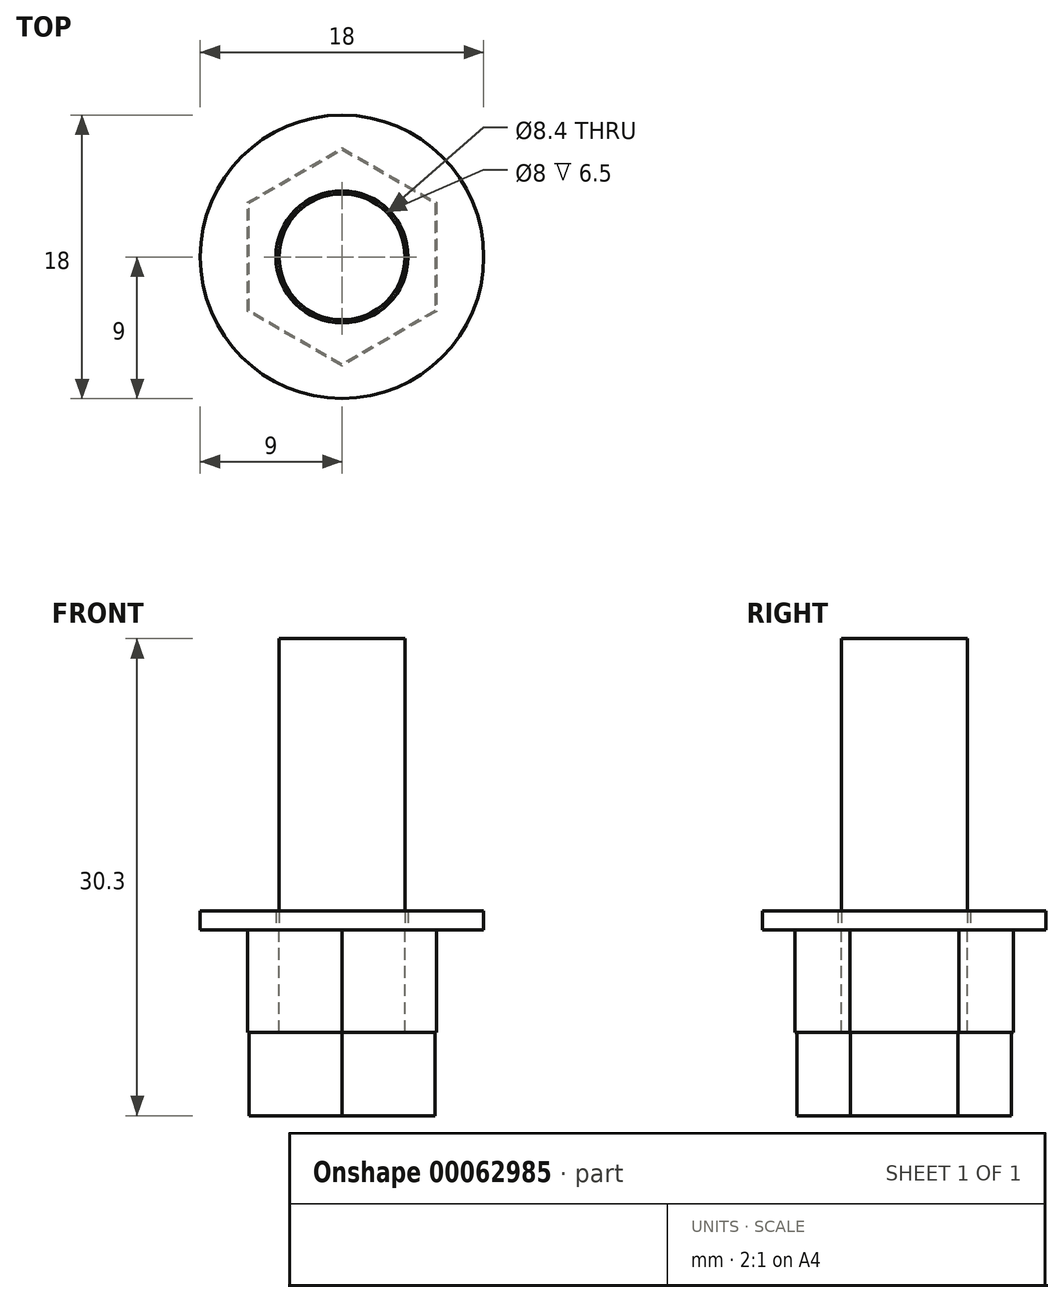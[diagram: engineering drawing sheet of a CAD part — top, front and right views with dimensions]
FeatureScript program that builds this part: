
annotation { "Feature Type Name" : "Feature", "Feature Type Description" : "" }
export const myFeature = defineFeature(function(context is Context, id is Id, definition is map)
    precondition{}
    {
        {
            var Q0;
            Q0=qCreatedBy(makeId("Top.planeOp"),FACE);
            var sketch = newSketch(context, id + "F0", { "sketchPlane" : qUnion([Q0])});
            skCircle(sketch, "E0.cCircle", {"center": v(0, 0) * mm, "radius": 5.9 * mm, "construction": true});
            skLineSegment(sketch, "E0.0", {"start": v(5.9, -3.4) * mm, "end": v(0, -6.81) * mm});
            skLineSegment(sketch, "E0.1", {"start": v(0, -6.81) * mm, "end": v(-5.9, -3.4) * mm});
            skLineSegment(sketch, "E0.2", {"start": v(-5.9, -3.4) * mm, "end": v(-5.9, 3.4) * mm});
            skLineSegment(sketch, "E0.3", {"start": v(-5.9, 3.4) * mm, "end": v(0, 6.81) * mm});
            skLineSegment(sketch, "E0.4", {"start": v(0, 6.81) * mm, "end": v(5.9, 3.4) * mm});
            skLineSegment(sketch, "E0.5", {"start": v(5.9, 3.4) * mm, "end": v(5.9, -3.4) * mm});
            skPoint(sketch, "E0.0.midPoint", {"position": v(2.95, -5.1) * mm});
            skSolve(sketch);
        }
        {
            var Q0;
            Q0=makeQuery(id+"F0.imprint","IMPRINT",FACE,{"disambiguationData":[TD([[makeQuery(id+"F0.imprint","IMPRINT",EDGE,{"derivedFrom":sQuery(id+"F0.wireOp",EDGE,"E0.0")}),-1.0]])]});
            extrude(context, id + "F1", {"entities" : qUnion([Q0]), "depth" : 5.3 * mm});
        }
        {
            var Q0;
            Q0=makeQuery(id+"F1.opExtrude","CAP_FACE",FACE,{"disambiguationData":[OSD([sQuery(id+"F0.wireOp",EDGE,"E0.0"),sQuery(id+"F0.wireOp",EDGE,"E0.1"),sQuery(id+"F0.wireOp",EDGE,"E0.2"),sQuery(id+"F0.wireOp",EDGE,"E0.3"),sQuery(id+"F0.wireOp",EDGE,"E0.4"),sQuery(id+"F0.wireOp",EDGE,"E0.5")])],"isStart":false});
            var sketch = newSketch(context, id + "F2", { "sketchPlane" : qUnion([Q0])});
            skCircle(sketch, "E1", {"center": v(0, 0) * mm, "radius": 4 * mm});
            skSolve(sketch);
        }
        {
            var Q0;
            Q0 = qSketchRegion(id + "F2", true);
            extrude(context, id + "F3", {"entities" : qUnion([Q0]), "operationType" : NewBodyOperationType.ADD, "depth" : 25 * mm});
        }
        {
            var Q0;
            Q0=makeQuery(id+"F1.opExtrude","CAP_FACE",FACE,{"disambiguationData":[OSD([sQuery(id+"F0.wireOp",EDGE,"E0.0"),sQuery(id+"F0.wireOp",EDGE,"E0.1"),sQuery(id+"F0.wireOp",EDGE,"E0.2"),sQuery(id+"F0.wireOp",EDGE,"E0.3"),sQuery(id+"F0.wireOp",EDGE,"E0.4"),sQuery(id+"F0.wireOp",EDGE,"E0.5")])],"isStart":false});
            var sketch = newSketch(context, id + "F4", { "sketchPlane" : qUnion([Q0])});
            skCircle(sketch, "E2.cCircle", {"center": v(0, 0) * mm, "radius": 6 * mm, "construction": true});
            skLineSegment(sketch, "E2.0", {"start": v(6, -3.46) * mm, "end": v(0, -6.93) * mm});
            skLineSegment(sketch, "E2.1", {"start": v(0, -6.93) * mm, "end": v(-6, -3.46) * mm});
            skLineSegment(sketch, "E2.2", {"start": v(-6, -3.46) * mm, "end": v(-6, 3.46) * mm});
            skLineSegment(sketch, "E2.3", {"start": v(-6, 3.46) * mm, "end": v(0, 6.93) * mm});
            skLineSegment(sketch, "E2.4", {"start": v(0, 6.93) * mm, "end": v(6, 3.46) * mm});
            skLineSegment(sketch, "E2.5", {"start": v(6, 3.46) * mm, "end": v(6, -3.46) * mm});
            skPoint(sketch, "E2.0.midPoint", {"position": v(3, -5.2) * mm});
            skSolve(sketch);
        }
        {
            var Q0;
            Q0 = qSketchRegion(id + "F4", true);
            extrude(context, id + "F5", {"entities" : qUnion([Q0]), "depth" : 6.5 * mm});
        }
        {
            var Q0;
            Q0=makeQuery(id+"F5.opExtrude","CAP_FACE",FACE,{"disambiguationData":[OSD([sQuery(id+"F4.wireOp",EDGE,"E2.0"),sQuery(id+"F4.wireOp",EDGE,"E2.1"),sQuery(id+"F4.wireOp",EDGE,"E2.2"),sQuery(id+"F4.wireOp",EDGE,"E2.3"),sQuery(id+"F4.wireOp",EDGE,"E2.4"),sQuery(id+"F4.wireOp",EDGE,"E2.5")])],"isStart":false});
            var sketch = newSketch(context, id + "F6", { "sketchPlane" : qUnion([Q0])});
            skCircle(sketch, "E3", {"center": v(0, 0) * mm, "radius": 4 * mm});
            skSolve(sketch);
        }
        {
            var Q0;
            Q0 = qSketchRegion(id + "F6", true);
            extrude(context, id + "F7", {"entities" : qUnion([Q0]), "operationType" : NewBodyOperationType.REMOVE, "oppositeDirection" : true, "depth" : 6.5 * mm});
        }
        {
            var Q0;
            Q0=makeQuery(id+"F5.opExtrude","CAP_FACE",FACE,{"disambiguationData":[OSD([sQuery(id+"F4.wireOp",EDGE,"E2.0"),sQuery(id+"F4.wireOp",EDGE,"E2.1"),sQuery(id+"F4.wireOp",EDGE,"E2.2"),sQuery(id+"F4.wireOp",EDGE,"E2.3"),sQuery(id+"F4.wireOp",EDGE,"E2.4"),sQuery(id+"F4.wireOp",EDGE,"E2.5")])],"isStart":false});
            var sketch = newSketch(context, id + "F8", { "sketchPlane" : qUnion([Q0])});
            skCircle(sketch, "E4", {"center": v(0, 0) * mm, "radius": 9 * mm});
            skCircle(sketch, "E5", {"center": v(0, 0) * mm, "radius": 4.2 * mm});
            skSolve(sketch);
        }
        {
            var Q0;
            Q0 = qSketchRegion(id + "F8", true);
            extrude(context, id + "F9", {"entities" : qUnion([Q0]), "depth" : 1.2 * mm});
        }
    });
